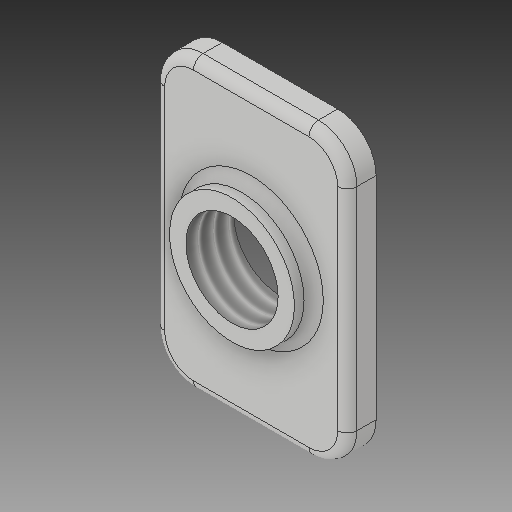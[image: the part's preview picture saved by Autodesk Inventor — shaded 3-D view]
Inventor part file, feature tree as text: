
AUTODESK INVENTOR PART (.ipt)
format: ipt  version: 2017 (Build 210142000, 142)  size: 175,104 bytes
history: native  units: mm
features: other x3, sketch x2
ambient origin geometry x8: Origin, YZ Plane, XZ Plane, XY Plane, X Axis, Y Axis, Z Axis, Center Point
bodies: Solid1 (feature_tree)
feature tree (5):
  other  "M5 Tee Nut-Generic_MIR.ipt"
  other  "Solid1::M5 Tee Nut-Generic_MIR.ipt"
  other  "TaggingFeature1"
  sketch  "Sketch1"  dims[d0=10.0mm]
  sketch  "Sketch2"
